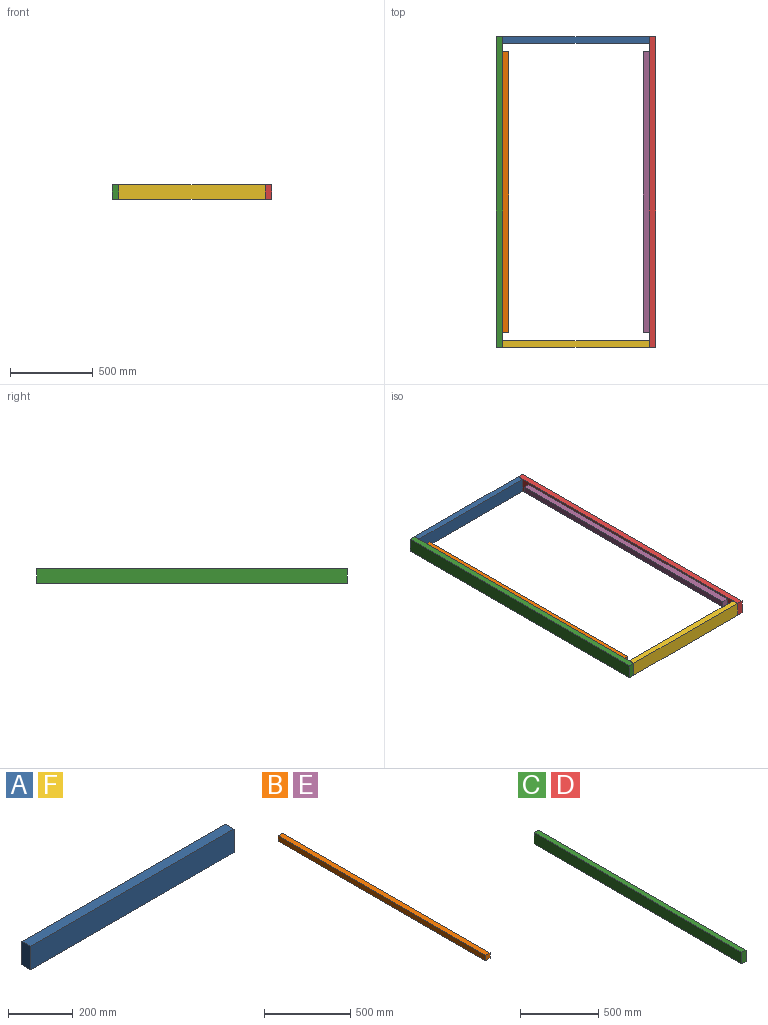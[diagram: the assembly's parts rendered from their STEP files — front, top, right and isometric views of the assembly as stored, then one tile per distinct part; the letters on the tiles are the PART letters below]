
ASSEMBLY  parts=6 mates=5
PART A: 6 faces, bbox 889x38.1x88.9 mm
  f0: plane 889x88.9mm, normal (0,1,0), area 79032.1mm2, adj f1,f3,f4,f5
  f1: plane 88.9x38.1mm, normal (-1,0,0), area 3387.1mm2, adj f0,f2,f4,f5
  f2: plane 889x88.9mm, normal (0,-1,0), area 79032.1mm2, adj f1,f3,f4,f5
  f3: plane 88.9x38.1mm, normal (1,0,0), area 3387.1mm2, adj f0,f2,f4,f5
  f4: plane 889x38.1mm, normal (0,0,1), area 33870.9mm2, adj f0,f1,f2,f3
  f5: plane 889x38.1mm, normal (0,0,-1), area 33870.9mm2, adj f0,f1,f2,f3
PART B: 6 faces, bbox 38.1x1701.8x38.1 mm
  f0: plane 1701.8x38.1mm, normal (0,0,1), area 64838.6mm2, adj f1,f2,f3,f4
  f1: plane 1701.8x38.1mm, normal (1,0,0), area 64838.6mm2, adj f0,f2,f3,f5
  f2: plane 38.1x38.1mm, normal (0,-1,0), area 1451.6mm2, adj f0,f1,f4,f5
  f3: plane 38.1x38.1mm, normal (0,1,0), area 1451.6mm2, adj f0,f1,f4,f5
  f4: plane 1701.8x38.1mm, normal (-1,0,0), area 64838.6mm2, adj f0,f2,f3,f5
  f5: plane 1701.8x38.1mm, normal (0,0,-1), area 64838.6mm2, adj f1,f2,f3,f4
PART C: 6 faces, bbox 38.1x1879.6x88.9 mm
  f0: plane 1879.6x88.9mm, normal (-1,0,0), area 167096.4mm2, adj f1,f3,f4,f5
  f1: plane 88.9x38.1mm, normal (0,-1,0), area 3387.1mm2, adj f0,f2,f4,f5
  f2: plane 1879.6x88.9mm, normal (1,0,0), area 167096.4mm2, adj f1,f3,f4,f5
  f3: plane 88.9x38.1mm, normal (0,1,0), area 3387.1mm2, adj f0,f2,f4,f5
  f4: plane 1879.6x38.1mm, normal (0,0,1), area 71612.8mm2, adj f0,f1,f2,f3
  f5: plane 1879.6x38.1mm, normal (0,0,-1), area 71612.8mm2, adj f0,f1,f2,f3
PART D: same geometry as C
PART E: same geometry as B
PART F: same geometry as A
PLACE A t=(941.87,-404.69,-1603.12)mm
PLACE B t=(90.97,-404.69,-1603.12)mm
PLACE C t=(14.77,-404.69,-1603.12)mm
PLACE D t=(941.87,-404.69,-1603.12)mm
PLACE E t=(941.87,-404.69,-1603.12)mm
PLACE F t=(941.87,-2246.19,-1603.12)mm
MATE fastened C.f2 <-> A.f1  axis (1,0,0) through (-480.53,1208.21,-9.27)mm
MATE fastened F.f3 <-> D.f0  axis (1,0,0) through (408.47,-671.39,-9.27)mm
MATE fastened F.f1 <-> C.f2  axis (-1,0,0) through (-480.53,-671.39,-9.27)mm
MATE fastened C.f2 <-> B.f4  axis (1,0,0) through (-480.53,268.41,35.18)mm
MATE fastened E.f1 <-> D.f0  axis (1,0,0) through (408.47,268.41,22.48)mm
